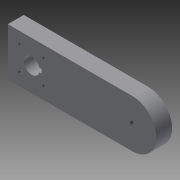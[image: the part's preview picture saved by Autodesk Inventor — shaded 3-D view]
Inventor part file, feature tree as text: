
AUTODESK INVENTOR PART (.ipt)
format: ipt  version: 2015 SP1 (Build 190203100, 203)  size: 108,544 bytes
history: native  units: in
note: dims shown in document units (in); Inventor stores cm internally (conversion verified against a paired STEP export)
features: sketch x3, hole x2, extrude x1
ambient origin geometry x8: Origin, YZ Plane, XZ Plane, XY Plane, X Axis, Y Axis, Z Axis, Center Point
bodies: Body1 (feature_tree)
feature tree (6):
  extrude  "Extrusion2"  Depth=1.0in
  hole  "Hole1"  [1 undecoded]
  hole  "Hole3"  [1 undecoded]
  sketch  "Sketch1"  dims[d0=3.0in d4=1.0in]
  sketch  "Sketch2"  dims[d13=0.1in d14=0.25in]
  sketch  "Sketch4"  dims[d15=6.3in d16=0.13in d17=1.5in d18=1.0in d19=0.0in d20=1.5in d21=1.5in d22=0.75in d23=0.75in d24=0.196in d25=0.75in d26=0.375in d27=0.25in d28=0.5635in d29=1.0in d30=0.8108in d38=0.307in d39=0.75in d40=0.375in d41=0.25in d42=0.5635in d43=1.063in d44=0.8108in]
note: 2 required parameter values undecoded (feature->parameter linkage not recoverable at this tier; creation-order binding heuristic only, values carry confidence <= 0.55)
